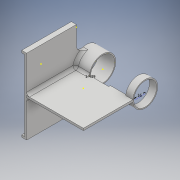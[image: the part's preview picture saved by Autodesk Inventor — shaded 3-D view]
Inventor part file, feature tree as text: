
AUTODESK INVENTOR PART (.ipt)
format: ipt  version: 2018 (Build 220112000, 112)  size: 224,768 bytes
history: native  units: mm
features: sketch x11, extrude x7, fillet x2
ambient origin geometry x8: Origin, YZ Plane, XZ Plane, XY Plane, X Axis, Y Axis, Z Axis, Center Point
bodies: Solid1 (feature_tree)
feature tree (20):
  extrude  "Extrusion1"  Depth=3.0mm
  extrude  "Extrusion2"  Depth=70.0mm
  extrude  "Extrusion3"  Depth=3.0mm TaperAngle=0.0deg
  sketch  "Sketch4"  dims[d9=17.0mm d10=34.0mm d11=37.0mm]
  extrude  "Extrusion4"  Depth=34.0mm
  fillet  "Fillet1"  Radius=37.0mm
  extrude  "Extrusion5"  Depth=10.0mm
  fillet  "Fillet2"  Radius=3.0mm
  extrude  "Extrusion6"  Depth=4.0mm
  sketch  "Sketch8"  dims[d23=2.439mm d24=0.0mm]
  sketch  "Sketch9"  dims[d25=16.0mm]
  sketch  "Sketch10"  dims[d26=1.439089mm]
  extrude  "Extrusion7"  Depth=50.0mm
  sketch  "Sketch1"  dims[d0=3.0mm d1=100.0mm]
  sketch  "Sketch2"  dims[d2=70.0mm d3=0.0mm d4=7.0mm]
  sketch  "Sketch3"  dims[d5=3.0mm d6=0.0mm d7=3.0mm d8=0.0mm]
  sketch  "Sketch5"  dims[d12=20.0mm d13=3.0mm d14=0.0mm d15=0.0mm d16=10.0mm d17=3.0mm]
  sketch  "Sketch6"  dims[d18=80.0mm d19=0.0mm d20=4.0mm]
  sketch  "Sketch7"  dims[d21=50.0mm d22=50.0mm]
  sketch  "Sketch11"  dims[d27=16.0mm d28=32.0mm d29=35.0mm d30=10.0mm d31=0.0mm]
